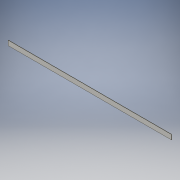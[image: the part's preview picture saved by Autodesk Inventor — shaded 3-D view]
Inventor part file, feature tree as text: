
AUTODESK INVENTOR PART (.ipt)
format: ipt  version: 2018 (Build 220112000, 112)  size: 94,208 bytes
history: native  units: mm
features: extrude x1, sketch x1
ambient origin geometry x8: Origin, YZ Plane, XZ Plane, XY Plane, X Axis, Y Axis, Z Axis, Center Point
bodies: Solid1 (feature_tree)
feature tree (2):
  extrude  "Extrusion1"  Depth=40.0mm
  sketch  "Sketch1"  dims[d0=1400.0mm d1=40.0mm d2=2.5mm d3=0.0mm]
